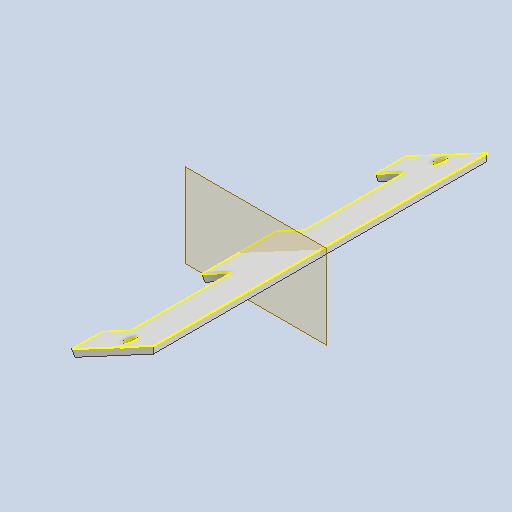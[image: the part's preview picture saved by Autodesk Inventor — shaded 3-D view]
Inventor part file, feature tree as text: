
AUTODESK INVENTOR PART (.ipt)
format: ipt  version: 2023 (Build 270158000, 158)  size: 311,296 bytes
history: native  units: in
note: dims shown in document units (in); Inventor stores cm internally (conversion verified against a paired STEP export)
features: other x10, reference x8, sketch x5, extrude x4, projected_geometry x2, mirror x1
ambient origin geometry x8: Origin, YZ Plane, XZ Plane, XY Plane, X Axis, Y Axis, Z Axis, Center Point
bodies: Body1 (feature_tree)
feature tree (30):
  other  "Bryła1"
  extrude  "Wyciągnięcie proste1"  Depth=3.937in
  extrude  "Wyciągnięcie proste4"  Depth=3.937in TaperAngle=0.0deg
  other  "Płaszczyzna konstrukcyjna1"
  mirror  "Odbij1"
  extrude  "Wyciągnięcie proste5"  Depth=0.0197in
  extrude  "Wyciągnięcie proste6"  Depth=0.0197in
  sketch  "Szkic8"
  sketch  "Szkic1"
  reference  "Odniesienie1"
  reference  "Odniesienie2"
  reference  "Odniesienie3"
  reference  "Odniesienie4"
  sketch  "Szkic5"
  reference  "Odniesienie15"
  reference  "Odniesienie16"
  reference  "Odniesienie17"
  sketch  "Szkic6"
  reference  "Odniesienie18"
  sketch  "Szkic7"
  projected_geometry  "Pętla rzutowana3"
  projected_geometry  "Pętla rzutowana4"
  other  "<userpath>\Desktop\PULPIT\MojeRoboty\Stefan\mechanics 2\STEFAN.iam"
  other  "STEFAN.iam"
  other  "podstawa:1"
  other  "<userpath>\Desktop\MojeRoboty\Stefan\mechanics 2\STEFAN.iam"
  other  "koło_minisumo:2"
  other  "plug_nowy:1"
  other  "mocowanie sharpow:1"
  other  "plug_kopia:1"
